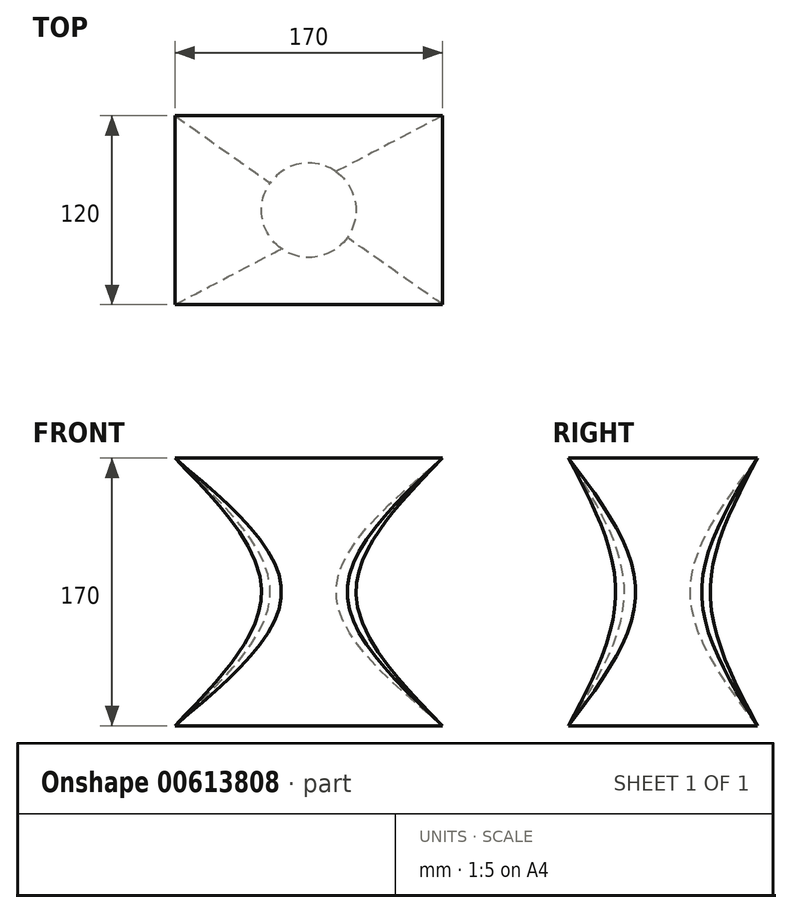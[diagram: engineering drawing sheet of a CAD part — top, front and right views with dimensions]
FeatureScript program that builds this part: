
annotation { "Feature Type Name" : "Feature", "Feature Type Description" : "" }
export const myFeature = defineFeature(function(context is Context, id is Id, definition is map)
    precondition{}
    {
        {
            var Q0;
            Q0=qCreatedBy(makeId("Top.planeOp"),FACE);
            var sketch = newSketch(context, id + "F0", { "sketchPlane" : qUnion([Q0])});
            skLineSegment(sketch, "E0.bottom", {"start": v(-85, 60) * mm, "end": v(85, 60) * mm});
            skLineSegment(sketch, "E0.top", {"start": v(-85, -60) * mm, "end": v(85, -60) * mm});
            skLineSegment(sketch, "E0.left", {"start": v(-85, 60) * mm, "end": v(-85, -60) * mm});
            skLineSegment(sketch, "E0.right", {"start": v(85, 60) * mm, "end": v(85, -60) * mm});
            skPoint(sketch, "E0.middle", {"position": v(0, 0) * mm});
            skSolve(sketch);
        }
        {
            var Q0;
            Q0=qCreatedBy(makeId("Top.planeOp"),FACE);
            cPlane(context, id + "F1", {"entities" : qUnion([Q0]), "cplaneType" : CPlaneType.OFFSET, "offset" : 170 * mm, "width" : 150 * mm, "height" : 150 * mm});
        }
        {
            var Q0;
            Q0=qCreatedBy(id+"F1.planeOp",FACE);
            var sketch = newSketch(context, id + "F2", { "sketchPlane" : qUnion([Q0])});
            skLineSegment(sketch, "E1.bottom", {"start": v(-85, 60) * mm, "end": v(85, 60) * mm});
            skLineSegment(sketch, "E1.top", {"start": v(-85, -60) * mm, "end": v(85, -60) * mm});
            skLineSegment(sketch, "E1.left", {"start": v(-85, 60) * mm, "end": v(-85, -60) * mm});
            skLineSegment(sketch, "E1.right", {"start": v(85, 60) * mm, "end": v(85, -60) * mm});
            skPoint(sketch, "E1.middle", {"position": v(0, 0) * mm});
            skSolve(sketch);
        }
        {
            var Q0;
            Q0=qCreatedBy(makeId("Top.planeOp"),FACE);
            cPlane(context, id + "F3", {"entities" : qUnion([Q0]), "cplaneType" : CPlaneType.OFFSET, "offset" : 85 * mm, "width" : 150 * mm, "height" : 150 * mm});
        }
        {
            var Q0;
            Q0=qCreatedBy(id+"F3.planeOp",FACE);
            var sketch = newSketch(context, id + "F4", { "sketchPlane" : qUnion([Q0])});
            skCircle(sketch, "E2", {"center": v(0, 0) * mm, "radius": 30 * mm});
            skSolve(sketch);
        }
        {
            var Q0;
            Q0 = qSketchRegion(id + "F0", true);
            var Q1;
            Q1 = qSketchRegion(id + "F4", true);
            var Q2;
            Q2 = qSketchRegion(id + "F2", true);
            loft(context, id + "F5", {"sheetProfilesArray" : [{ "sheetProfileEntities" : qUnion([Q0]) }, { "sheetProfileEntities" : qUnion([Q1]) }, { "sheetProfileEntities" : qUnion([Q2]) }]});
        }
    });
